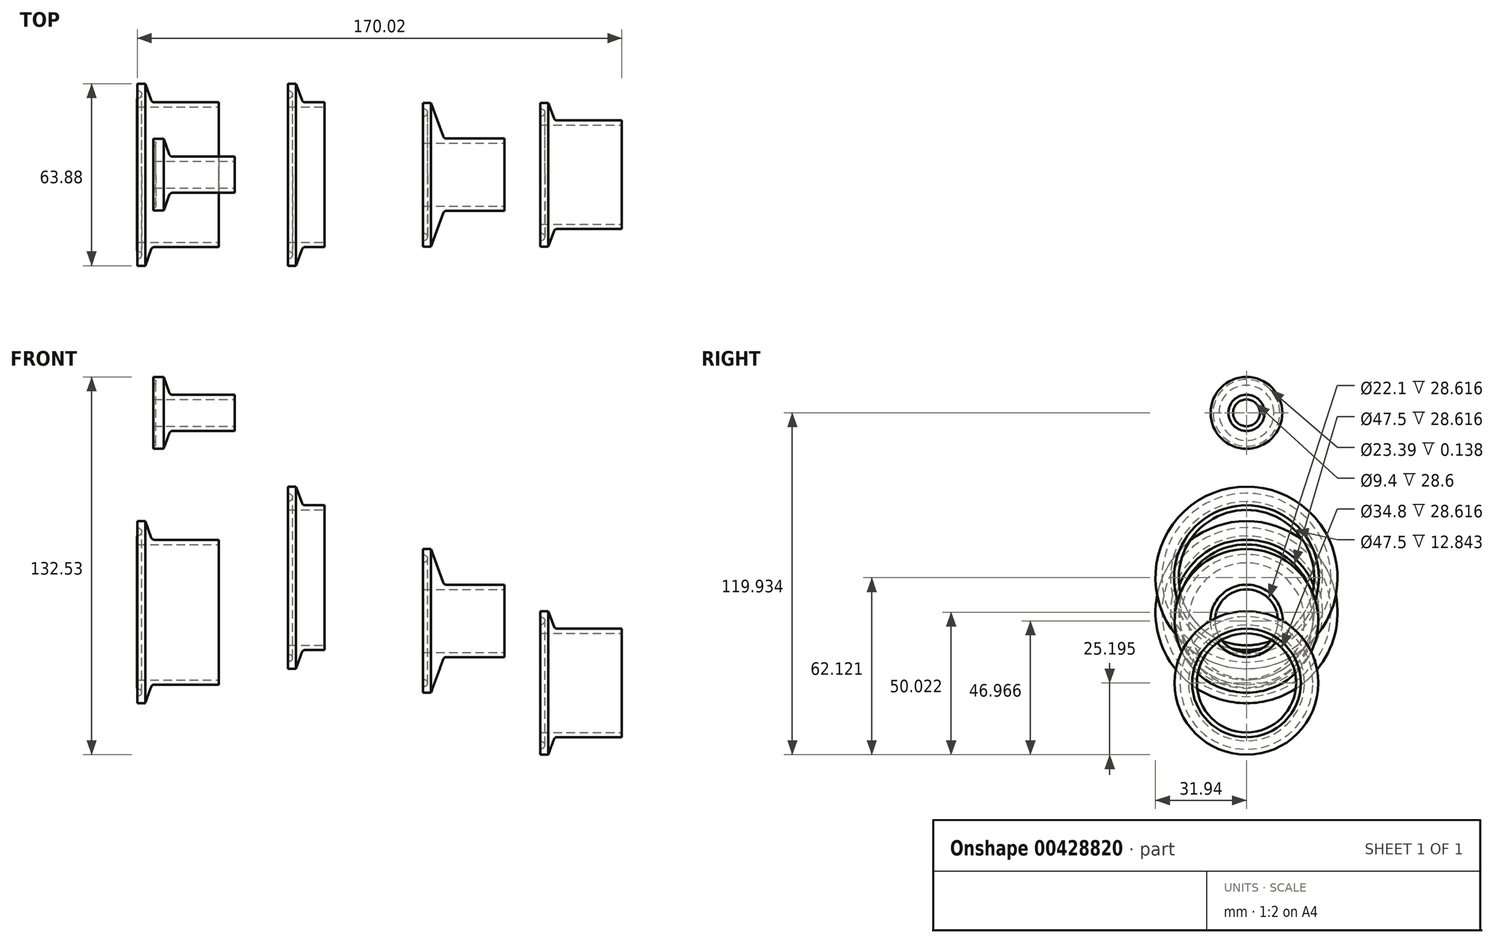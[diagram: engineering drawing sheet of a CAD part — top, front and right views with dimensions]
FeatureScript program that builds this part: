
annotation { "Feature Type Name" : "Feature", "Feature Type Description" : "" }
export const myFeature = defineFeature(function(context is Context, id is Id, definition is map)
    precondition{}
    {
        {
            var Q0;
            Q0=qCreatedBy(makeId("Front.planeOp"),FACE);
            var sketch = newSketch(context, id + "F0", { "sketchPlane" : qUnion([Q0])});
            skLineSegment(sketch, "E0", {"start": v(-12.83, 14.73) * mm, "end": v(-10.02, 14.73) * mm});
            skLineSegment(sketch, "E1", {"start": v(-10.02, 14.73) * mm, "end": v(-7.64, 8.2) * mm, "construction": true});
            skLineSegment(sketch, "E2", {"start": v(-7.64, 8.2) * mm, "end": v(0, 8.2) * mm, "construction": true});
            skLineSegment(sketch, "E3", {"start": v(0, 8.2) * mm, "end": v(0, -17.2) * mm});
            skLineSegment(sketch, "E4", {"start": v(0, -17.2) * mm, "end": v(-12.78, -17.2) * mm, "construction": true});
            skLineSegment(sketch, "E5", {"start": v(-11.21, 14.73) * mm, "end": v(-11.21, -17.2) * mm, "construction": true});
            skLineSegment(sketch, "E6", {"start": v(0, 6.54) * mm, "end": v(-12.84, 6.54) * mm});
            skArc(sketch, "E7", {"start": v(-7.91, 8.94) * mm, "mid": v(-7.5, 8.4) * mm, "end": v(-6.84, 8.2) * mm});
            skLineSegment(sketch, "E8", {"start": v(-12.83, 12.44) * mm, "end": v(-11.21, 11.75) * mm, "construction": true});
            skLineSegment(sketch, "E9", {"start": v(-12.84, 9.48) * mm, "end": v(-11.21, 10.17) * mm, "construction": true});
            skArc(sketch, "E10", {"start": v(-11.21, 10.96) * mm, "mid": v(-11.4, 11.62) * mm, "end": v(-11.94, 12.06) * mm});
            skArc(sketch, "E11", {"start": v(-11.94, 9.86) * mm, "mid": v(-11.4, 10.3) * mm, "end": v(-11.21, 10.96) * mm});
            skLineSegment(sketch, "E12", {"start": v(-12.83, 14.73) * mm, "end": v(-12.83, 12.44) * mm});
            skLineSegment(sketch, "E13", {"start": v(-12.84, 9.48) * mm, "end": v(-12.84, 6.54) * mm});
            skLineSegment(sketch, "E14", {"start": v(-7.91, 8.94) * mm, "end": v(-10.02, 14.73) * mm});
            skLineSegment(sketch, "E15", {"start": v(-6.84, 8.2) * mm, "end": v(0, 8.2) * mm});
            skLineSegment(sketch, "E16", {"start": v(-12.83, 12.44) * mm, "end": v(-11.94, 12.06) * mm});
            skLineSegment(sketch, "E17", {"start": v(-12.84, 9.48) * mm, "end": v(-11.94, 9.86) * mm});
            skLineSegment(sketch, "E18", {"start": v(-11.21, 10.96) * mm, "end": v(-11.21, 10.96) * mm});
            skLineSegment(sketch, "E19", {"start": v(-11.21, 10.96) * mm, "end": v(-16.43, 10.96) * mm, "construction": true});
            skSolve(sketch);
        }
        {
            var Q0;
            Q0=qSketchRegion(id+"F0",true);
            var Q1;
            Q1=sQuery(id+"F0.wireOp",EDGE,"E4");
            revolve(context, id + "F1", {"entities" : qUnion([Q0]), "axis" : qUnion([Q1]), "revolveType" : RevolveType.FULL});
        }
        {
            var Q0;
            Q0=qCreatedBy(makeId("Front.planeOp"),FACE);
            var sketch = newSketch(context, id + "F2", { "sketchPlane" : qUnion([Q0])});
            skLineSegment(sketch, "E20", {"start": v(-65.7, 2.63) * mm, "end": v(-62.89, 2.63) * mm});
            skLineSegment(sketch, "E21", {"start": v(-62.89, 2.63) * mm, "end": v(-60.5, -3.9) * mm, "construction": true});
            skLineSegment(sketch, "E22", {"start": v(-60.5, -3.9) * mm, "end": v(-37.1, -3.9) * mm, "construction": true});
            skLineSegment(sketch, "E23", {"start": v(-37.1, -3.9) * mm, "end": v(-37.1, -29.3) * mm});
            skLineSegment(sketch, "E24", {"start": v(-37.1, -29.3) * mm, "end": v(-64.08, -29.3) * mm, "construction": true});
            skLineSegment(sketch, "E25", {"start": v(-64.08, 2.63) * mm, "end": v(-64.08, -29.3) * mm, "construction": true});
            skLineSegment(sketch, "E26", {"start": v(-37.1, -5.56) * mm, "end": v(-65.71, -5.56) * mm});
            skArc(sketch, "E27", {"start": v(-60.78, -3.16) * mm, "mid": v(-60.36, -3.7) * mm, "end": v(-59.7, -3.9) * mm});
            skLineSegment(sketch, "E28", {"start": v(-65.7, 0.34) * mm, "end": v(-64.08, -0.35) * mm, "construction": true});
            skLineSegment(sketch, "E29", {"start": v(-65.71, -2.62) * mm, "end": v(-64.08, -1.93) * mm, "construction": true});
            skArc(sketch, "E30", {"start": v(-64.08, -1.14) * mm, "mid": v(-64.28, -0.48) * mm, "end": v(-64.8, -0.04) * mm});
            skArc(sketch, "E31", {"start": v(-64.8, -2.24) * mm, "mid": v(-64.28, -1.8) * mm, "end": v(-64.08, -1.14) * mm});
            skLineSegment(sketch, "E32", {"start": v(-65.7, 2.63) * mm, "end": v(-65.7, 0.34) * mm});
            skLineSegment(sketch, "E33", {"start": v(-65.71, -2.62) * mm, "end": v(-65.71, -5.56) * mm});
            skLineSegment(sketch, "E34", {"start": v(-60.78, -3.16) * mm, "end": v(-62.89, 2.63) * mm});
            skLineSegment(sketch, "E35", {"start": v(-59.7, -3.9) * mm, "end": v(-37.1, -3.9) * mm});
            skLineSegment(sketch, "E36", {"start": v(-65.7, 0.34) * mm, "end": v(-64.8, -0.04) * mm});
            skLineSegment(sketch, "E37", {"start": v(-65.71, -2.62) * mm, "end": v(-64.8, -2.24) * mm});
            skLineSegment(sketch, "E38", {"start": v(-64.08, -1.14) * mm, "end": v(-64.08, -1.14) * mm});
            skLineSegment(sketch, "E39", {"start": v(-64.08, -1.14) * mm, "end": v(-65.71, -1.14) * mm, "construction": true});
            skSolve(sketch);
        }
        {
            var Q0;
            Q0=qSketchRegion(id+"F2",true);
            var Q1;
            Q1=sQuery(id+"F2.wireOp",EDGE,"E24");
            revolve(context, id + "F3", {"entities" : qUnion([Q0]), "axis" : qUnion([Q1]), "revolveType" : RevolveType.FULL});
        }
        {
            var Q0;
            Q0=qCreatedBy(makeId("Front.planeOp"),FACE);
            var sketch = newSketch(context, id + "F4", { "sketchPlane" : qUnion([Q0])});
            skLineSegment(sketch, "E40", {"start": v(34.56, -7.17) * mm, "end": v(37.36, -7.17) * mm});
            skLineSegment(sketch, "E41", {"start": v(37.36, -7.17) * mm, "end": v(41.91, -19.66) * mm, "construction": true});
            skLineSegment(sketch, "E42", {"start": v(41.91, -19.66) * mm, "end": v(63.16, -19.66) * mm, "construction": true});
            skLineSegment(sketch, "E43", {"start": v(63.16, -19.66) * mm, "end": v(63.16, -32.36) * mm});
            skLineSegment(sketch, "E44", {"start": v(63.16, -32.36) * mm, "end": v(36.17, -32.36) * mm, "construction": true});
            skLineSegment(sketch, "E45", {"start": v(36.17, -7.17) * mm, "end": v(36.17, -32.36) * mm, "construction": true});
            skLineSegment(sketch, "E46", {"start": v(63.16, -21.31) * mm, "end": v(34.54, -21.31) * mm});
            skArc(sketch, "E47", {"start": v(41.64, -18.91) * mm, "mid": v(42.06, -19.46) * mm, "end": v(42.71, -19.66) * mm});
            skLineSegment(sketch, "E48", {"start": v(34.56, -9.07) * mm, "end": v(36.17, -9.75) * mm, "construction": true});
            skLineSegment(sketch, "E49", {"start": v(34.54, -12.03) * mm, "end": v(36.17, -11.34) * mm, "construction": true});
            skArc(sketch, "E50", {"start": v(36.17, -10.55) * mm, "mid": v(35.97, -9.89) * mm, "end": v(35.45, -9.45) * mm});
            skArc(sketch, "E51", {"start": v(35.45, -11.64) * mm, "mid": v(35.97, -11.2) * mm, "end": v(36.17, -10.55) * mm});
            skLineSegment(sketch, "E52", {"start": v(34.56, -7.17) * mm, "end": v(34.56, -9.07) * mm});
            skLineSegment(sketch, "E53", {"start": v(34.54, -12.03) * mm, "end": v(34.54, -21.31) * mm});
            skLineSegment(sketch, "E54", {"start": v(41.64, -18.91) * mm, "end": v(37.36, -7.17) * mm});
            skLineSegment(sketch, "E55", {"start": v(42.71, -19.66) * mm, "end": v(63.16, -19.66) * mm});
            skLineSegment(sketch, "E56", {"start": v(34.56, -9.07) * mm, "end": v(35.45, -9.45) * mm});
            skLineSegment(sketch, "E57", {"start": v(34.54, -12.03) * mm, "end": v(35.45, -11.64) * mm});
            skLineSegment(sketch, "E58", {"start": v(36.17, -10.55) * mm, "end": v(36.17, -10.55) * mm});
            skLineSegment(sketch, "E59", {"start": v(36.17, -10.55) * mm, "end": v(34.54, -10.55) * mm, "construction": true});
            skSolve(sketch);
        }
        {
            var Q0;
            Q0=makeQuery(id+"F4.imprint","IMPRINT",FACE,{"disambiguationData":[TD([[makeQuery(id+"F4.imprint","IMPRINT",EDGE,{"derivedFrom":sQuery(id+"F4.wireOp",EDGE,"E40")}),-1.0]])]});
            var Q1;
            Q1=sQuery(id+"F4.wireOp",EDGE,"E44");
            revolve(context, id + "F5", {"entities" : qUnion([Q0]), "axis" : qUnion([Q1]), "revolveType" : RevolveType.FULL});
        }
        {
            var Q0;
            Q0=qCreatedBy(makeId("Front.planeOp"),FACE);
            var sketch = newSketch(context, id + "F6", { "sketchPlane" : qUnion([Q0])});
            skLineSegment(sketch, "E60", {"start": v(75.7, -28.94) * mm, "end": v(78.52, -28.94) * mm});
            skLineSegment(sketch, "E61", {"start": v(78.52, -28.94) * mm, "end": v(80.75, -35.08) * mm, "construction": true});
            skLineSegment(sketch, "E62", {"start": v(80.75, -35.08) * mm, "end": v(104.3, -35.08) * mm, "construction": true});
            skLineSegment(sketch, "E63", {"start": v(104.3, -35.08) * mm, "end": v(104.3, -54.13) * mm});
            skLineSegment(sketch, "E64", {"start": v(104.3, -54.13) * mm, "end": v(77.33, -54.13) * mm, "construction": true});
            skLineSegment(sketch, "E65", {"start": v(77.33, -28.94) * mm, "end": v(77.33, -54.13) * mm, "construction": true});
            skLineSegment(sketch, "E66", {"start": v(104.3, -36.74) * mm, "end": v(75.7, -36.74) * mm});
            skArc(sketch, "E67", {"start": v(80.48, -34.33) * mm, "mid": v(80.9, -34.88) * mm, "end": v(81.55, -35.08) * mm});
            skLineSegment(sketch, "E68", {"start": v(75.7, -30.84) * mm, "end": v(77.33, -31.53) * mm, "construction": true});
            skLineSegment(sketch, "E69", {"start": v(75.7, -33.8) * mm, "end": v(77.33, -33.1) * mm, "construction": true});
            skArc(sketch, "E70", {"start": v(77.33, -32.32) * mm, "mid": v(77.13, -31.66) * mm, "end": v(76.6, -31.22) * mm});
            skArc(sketch, "E71", {"start": v(76.6, -33.41) * mm, "mid": v(77.13, -32.97) * mm, "end": v(77.33, -32.32) * mm});
            skLineSegment(sketch, "E72", {"start": v(75.7, -28.94) * mm, "end": v(75.7, -30.84) * mm});
            skLineSegment(sketch, "E73", {"start": v(75.7, -33.8) * mm, "end": v(75.7, -36.74) * mm});
            skLineSegment(sketch, "E74", {"start": v(80.48, -34.33) * mm, "end": v(78.52, -28.94) * mm});
            skLineSegment(sketch, "E75", {"start": v(81.55, -35.08) * mm, "end": v(104.3, -35.08) * mm});
            skLineSegment(sketch, "E76", {"start": v(75.7, -30.84) * mm, "end": v(76.6, -31.22) * mm});
            skLineSegment(sketch, "E77", {"start": v(75.7, -33.8) * mm, "end": v(76.6, -33.41) * mm});
            skLineSegment(sketch, "E78", {"start": v(77.33, -32.32) * mm, "end": v(77.33, -32.32) * mm});
            skLineSegment(sketch, "E79", {"start": v(77.33, -32.32) * mm, "end": v(75.7, -32.32) * mm, "construction": true});
            skSolve(sketch);
        }
        {
            var Q0;
            Q0=qSketchRegion(id+"F6",true);
            var Q1;
            Q1=sQuery(id+"F6.wireOp",EDGE,"E64");
            revolve(context, id + "F7", {"entities" : qUnion([Q0]), "axis" : qUnion([Q1]), "revolveType" : RevolveType.FULL});
        }
        {
            var Q0;
            Q0=qCreatedBy(makeId("Front.planeOp"),FACE);
            var sketch = newSketch(context, id + "F8", { "sketchPlane" : qUnion([Q0])});
            skLineSegment(sketch, "E80", {"start": v(-60.03, 53.2) * mm, "end": v(-56.4, 53.2) * mm});
            skLineSegment(sketch, "E81", {"start": v(-56.4, 53.2) * mm, "end": v(-54.13, 46.95) * mm, "construction": true});
            skLineSegment(sketch, "E82", {"start": v(-54.13, 46.95) * mm, "end": v(-31.43, 46.95) * mm, "construction": true});
            skLineSegment(sketch, "E83", {"start": v(-31.43, 46.95) * mm, "end": v(-31.43, 40.6) * mm});
            skLineSegment(sketch, "E84", {"start": v(-31.43, 40.6) * mm, "end": v(-59.1, 40.6) * mm, "construction": true});
            skLineSegment(sketch, "E85", {"start": v(-59.1, 53.2) * mm, "end": v(-59.1, 40.6) * mm, "construction": true});
            skLineSegment(sketch, "E86", {"start": v(-31.43, 45.3) * mm, "end": v(-60.03, 45.3) * mm});
            skArc(sketch, "E87", {"start": v(-54.4, 47.7) * mm, "mid": v(-53.98, 47.16) * mm, "end": v(-53.33, 46.95) * mm});
            skLineSegment(sketch, "E88", {"start": v(-60.03, 52.3) * mm, "end": v(-59.1, 52.3) * mm, "construction": true});
            skLineSegment(sketch, "E89", {"start": v(-60.03, 50.26) * mm, "end": v(-59.1, 51.19) * mm, "construction": true});
            skArc(sketch, "E90", {"start": v(-59.1, 51.51) * mm, "mid": v(-59.34, 52.07) * mm, "end": v(-59.9, 52.3) * mm});
            skArc(sketch, "E91", {"start": v(-59.34, 50.96) * mm, "mid": v(-59.17, 51.21) * mm, "end": v(-59.1, 51.51) * mm});
            skLineSegment(sketch, "E92", {"start": v(-60.03, 53.2) * mm, "end": v(-60.03, 52.3) * mm});
            skLineSegment(sketch, "E93", {"start": v(-60.03, 50.26) * mm, "end": v(-60.03, 45.3) * mm});
            skLineSegment(sketch, "E94", {"start": v(-54.4, 47.7) * mm, "end": v(-56.4, 53.2) * mm});
            skLineSegment(sketch, "E95", {"start": v(-53.33, 46.95) * mm, "end": v(-31.43, 46.95) * mm});
            skLineSegment(sketch, "E96", {"start": v(-60.03, 52.3) * mm, "end": v(-59.9, 52.3) * mm});
            skLineSegment(sketch, "E97", {"start": v(-60.03, 50.26) * mm, "end": v(-59.34, 50.96) * mm});
            skLineSegment(sketch, "E98", {"start": v(-59.1, 51.51) * mm, "end": v(-59.1, 51.51) * mm});
            skLineSegment(sketch, "E99", {"start": v(-59.1, 51.51) * mm, "end": v(-60.03, 51.51) * mm, "construction": true});
            skSolve(sketch);
        }
        {
            var Q0;
            Q0=makeQuery(id+"F8.imprint","IMPRINT",FACE,{"disambiguationData":[TD([[makeQuery(id+"F8.imprint","IMPRINT",EDGE,{"derivedFrom":sQuery(id+"F8.wireOp",EDGE,"E80")}),-1.0]])]});
            var Q1;
            Q1=sQuery(id+"F8.wireOp",EDGE,"E84");
            revolve(context, id + "F9", {"entities" : qUnion([Q0]), "axis" : qUnion([Q1]), "revolveType" : RevolveType.FULL});
        }
    });
